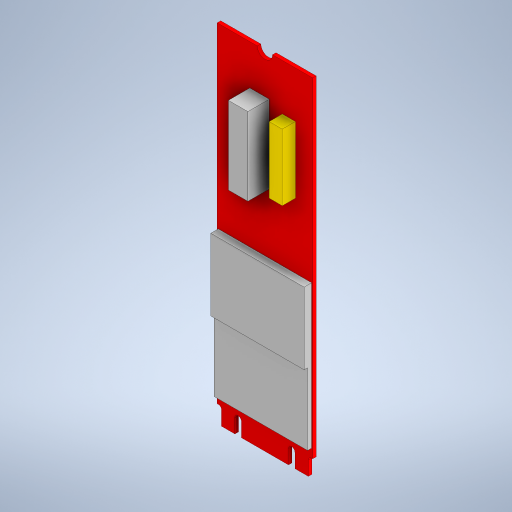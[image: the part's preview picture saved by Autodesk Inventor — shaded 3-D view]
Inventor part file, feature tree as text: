
AUTODESK INVENTOR PART (.ipt)
format: ipt  version: 2024 (Build 280153000, 153)  size: 407,040 bytes
history: native  units: mm
features: extrude x10, sketch x10, projected_geometry x4, fillet x1
ambient origin geometry x8: Origin, YZ Plane, XZ Plane, XY Plane, X Axis, Y Axis, Z Axis, Center Point
bodies: Solid1 (feature_tree), Solid2 (feature_tree), Solid3 (feature_tree), Solid5 (feature_tree), Solid6 (feature_tree), Solid7 (feature_tree)
feature tree (25):
  extrude  "Extrusion1"  Depth=80.0mm
  extrude  "Extrusion2"  Depth=1.0mm
  fillet  "Fillet1"  Radius=1.0mm
  extrude  "Extrusion3"  Depth=1.5mm
  extrude  "Extrusion4"  Depth=0.75mm
  extrude  "Extrusion5"  Depth=40.0mm
  extrude  "Extrusion6"  Depth=1.5mm
  extrude  "Extrusion7"  Depth=45.0mm
  extrude  "Extrusion8"  Depth=5.0mm TaperAngle=0.0deg
  extrude  "Extrusion9"  Depth=12.4mm TaperAngle=0.0deg
  extrude  "Extrusion10"  Depth=15.3mm
  sketch  "Sketch1"  dims[d0=22.0mm d1=80.0mm]
  sketch  "Sketch2"  dims[d2=0.8mm d3=0.0mm d4=1.0mm d5=1.0mm]
  projected_geometry  "Projected Loop1"
  sketch  "Sketch3"  dims[d6=4.0mm d7=1.5mm]
  projected_geometry  "Projected Loop2"
  sketch  "Sketch4"  dims[d9=0.8mm d10=0.0mm d11=0.75mm]
  sketch  "Sketch5"  dims[d12=5.2mm d13=40.0mm]
  projected_geometry  "Projected Loop3"
  sketch  "Sketch6"  dims[d14=11.6mm d15=0.0mm d16=1.5mm]
  sketch  "Sketch7"  dims[d17=1.5mm d18=45.0mm]
  sketch  "Sketch8"  dims[d19=2.2mm d20=0.0mm d21=5.0mm d22=0.0mm]
  sketch  "Sketch9"  dims[d23=3.5mm d24=12.4mm d25=0.0mm]
  sketch  "Sketch10"  dims[d26=3.0mm d27=15.3mm d28=10.7mm d29=4.0mm d30=3.0mm d31=0.0mm d32=4.5mm d36=3.0mm d37=4.93mm d38=0.0mm d39=4.825mm d40=33.0mm d42=6.0mm d43=0.25mm d44=0.25mm d45=1.73mm d46=0.0mm d47=9.25mm d48=17.9mm d49=0.8mm d50=0.0mm]
  projected_geometry  "Projected Loop4"
